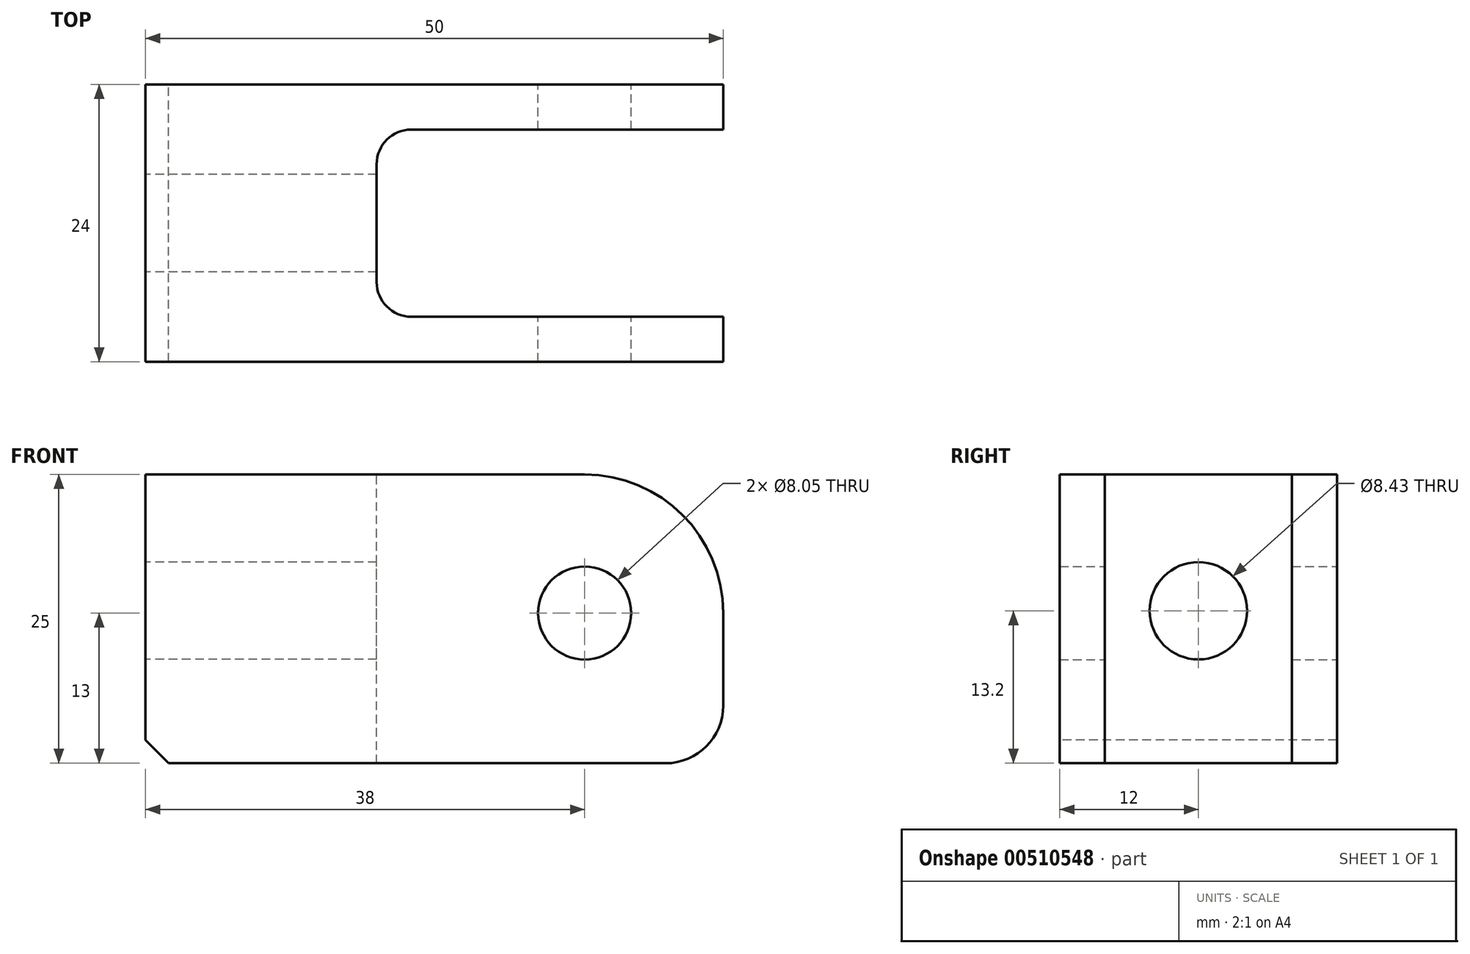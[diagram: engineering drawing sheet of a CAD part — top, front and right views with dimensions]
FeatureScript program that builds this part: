
annotation { "Feature Type Name" : "Feature", "Feature Type Description" : "" }
export const myFeature = defineFeature(function(context is Context, id is Id, definition is map)
    precondition{}
    {
        {
            var Q0;
            Q0=qCreatedBy(makeId("Front.planeOp"),FACE);
            var sketch = newSketch(context, id + "F0", { "sketchPlane" : qUnion([Q0])});
            skLineSegment(sketch, "E0.bottom", {"start": v(0, 0) * mm, "end": v(50, 0) * mm});
            skLineSegment(sketch, "E0.top", {"start": v(0, 25) * mm, "end": v(38, 25) * mm});
            skLineSegment(sketch, "E0.left", {"start": v(0, 0) * mm, "end": v(0, 25) * mm});
            skLineSegment(sketch, "E0.right", {"start": v(50, 0) * mm, "end": v(50, 13) * mm});
            skPoint(sketch, "E1.visualSharp", {"position": v(50, 25) * mm});
            skArc(sketch, "E1.filletArc", {"start": v(50, 13) * mm, "mid": v(46.49, 21.49) * mm, "end": v(38, 25) * mm});
            skCircle(sketch, "E2", {"center": v(38, 13) * mm, "radius": 4.03 * mm});
            skLineSegment(sketch, "E3.bottom", {"start": v(25, -10) * mm, "end": v(60, -10) * mm});
            skLineSegment(sketch, "E3.top", {"start": v(20, 40) * mm, "end": v(60, 40) * mm});
            skLineSegment(sketch, "E3.left", {"start": v(20, -5) * mm, "end": v(20, 40) * mm});
            skLineSegment(sketch, "E3.right", {"start": v(60, -10) * mm, "end": v(60, 40) * mm});
            skPoint(sketch, "E4.visualSharp", {"position": v(20, -10) * mm});
            skArc(sketch, "E4.filletArc", {"start": v(20, -5) * mm, "mid": v(21.46, -8.54) * mm, "end": v(25, -10) * mm});
            skSolve(sketch);
        }
        {
            var Q0;
            Q0=makeQuery(id+"F0.imprint","IMPRINT",FACE,{"disambiguationData":[TD([[makeQuery(id+"F0.imprint","IMPRINT",EDGE,{"derivedFrom":sQuery(id+"F0.wireOp",EDGE,"E0.bottom")}),1.0]])]});
            var Q1;
            {var subQ0=sQuery(id+"F0.wireOp",EDGE,"E1.filletArc");Q1=makeQuery(id+"F0.imprint","IMPRINT",FACE,{"disambiguationData":[TD([[makeQuery(id+"F0.imprint","IMPRINT",EDGE,{"derivedFrom":subQ0}),1.0]])]});}
            extrude(context, id + "F1", {"entities" : qUnion([Q0, Q1]), "depth" : 12 * mm, "hasSecondDirection" : true, "secondDirectionOppositeDirection" : true, "secondDirectionDepth" : 12 * mm});
        }
        {
            var Q0;
            {var subQ0=sQuery(id+"F0.wireOp",EDGE,"E1.filletArc");Q0=makeQuery(id+"F0.imprint","IMPRINT",FACE,{"disambiguationData":[TD([[makeQuery(id+"F0.imprint","IMPRINT",EDGE,{"derivedFrom":subQ0}),1.0]])]});}
            extrude(context, id + "F2", {"entities" : qUnion([Q0]), "operationType" : NewBodyOperationType.REMOVE, "oppositeDirection" : true, "depth" : 8.1 * mm, "hasSecondDirection" : true, "secondDirectionOppositeDirection" : false, "secondDirectionDepth" : 8.1 * mm, "offsetDistance" : 25 * mm});
        }
        {
            var Q0;
            Q0=makeQuery(id+"F2.boolean.opBoolean","COPY",EDGE,{"derivedFrom":makeQuery(id+"F2.opExtrude","CAP_EDGE",EDGE,{"disambiguationData":[OSD([sQuery(id+"F0.wireOp",EDGE,"E3.left")])],"isStart":true})});
            var Q1;
            Q1=makeQuery(id+"F2.boolean.opBoolean","COPY",EDGE,{"derivedFrom":makeQuery(id+"F2.opExtrude","CAP_EDGE",EDGE,{"disambiguationData":[OSD([sQuery(id+"F0.wireOp",EDGE,"E3.left")])],"isStart":false})});
            fillet(context, id + "F3", {"entities" : qUnion([Q0, Q1]), "radius" : 3 * mm, "tangentPropagation" : true, "allowEdgeOverflow" : false});
        }
        {
            var Q0;
            {var subQ0=sQuery(id+"F0.wireOp",EDGE,"E0.bottom");var subQ1=sQuery(id+"F0.wireOp",EDGE,"E0.right");var subQ2=sQuery(id+"F0.wireOp",EDGE,"E2");var subQ3=sQuery(id+"F0.wireOp",EDGE,"E1.filletArc");var subQ4=sQuery(id+"F0.wireOp",EDGE,"E0.top");Q0=makeQuery(id+"F2.boolean.opBoolean","SPLIT",EDGE,{"disambiguationData":[TD([makeQuery(id+"F1.opExtrude","CAP_FACE",FACE,{"disambiguationData":[OSD([subQ0,subQ4,sQuery(id+"F0.wireOp",EDGE,"E0.left"),subQ1,subQ3,subQ2])],"isStart":false})])],"derivedFrom":makeQuery(id+"F1.opExtrude","SWEPT_EDGE",EDGE,{"disambiguationData":[OSD([subQ0,subQ1])]})});}
            var Q1;
            {var subQ0=sQuery(id+"F0.wireOp",EDGE,"E0.bottom");var subQ1=sQuery(id+"F0.wireOp",EDGE,"E0.right");var subQ2=sQuery(id+"F0.wireOp",EDGE,"E2");var subQ3=sQuery(id+"F0.wireOp",EDGE,"E1.filletArc");var subQ4=sQuery(id+"F0.wireOp",EDGE,"E0.top");Q1=makeQuery(id+"F2.boolean.opBoolean","SPLIT",EDGE,{"disambiguationData":[TD([makeQuery(id+"F1.opExtrude","CAP_FACE",FACE,{"disambiguationData":[OSD([subQ0,subQ4,sQuery(id+"F0.wireOp",EDGE,"E0.left"),subQ1,subQ3,subQ2])],"isStart":true})])],"derivedFrom":makeQuery(id+"F1.opExtrude","SWEPT_EDGE",EDGE,{"disambiguationData":[OSD([subQ0,subQ1])]})});}
            fillet(context, id + "F4", {"entities" : qUnion([Q0, Q1]), "radius" : 5 * mm, "tangentPropagation" : true, "allowEdgeOverflow" : false});
        }
        {
            var Q0;
            Q0=makeQuery(id+"F1.opExtrude","SWEPT_FACE",FACE,{"disambiguationData":[OSD([sQuery(id+"F0.wireOp",EDGE,"E0.left")])]});
            var sketch = newSketch(context, id + "F5", { "sketchPlane" : qUnion([Q0])});
            skPoint(sketch, "E5", {"position": v(0, 13.2) * mm});
            skSolve(sketch);
        }
        {
            var Q0;
            Q0=sQuery(id+"F5.wireOp",VERTEX,"E5");
            var Q1;
            Q1=makeQuery(id+"F1.opExtrude","SWEPT_BODY",BODY,{"disambiguationData":[OSD([sQuery(id+"F0.wireOp",EDGE,"E0.bottom"),sQuery(id+"F0.wireOp",EDGE,"E0.top"),sQuery(id+"F0.wireOp",EDGE,"E0.left"),sQuery(id+"F0.wireOp",EDGE,"E0.right"),sQuery(id+"F0.wireOp",EDGE,"E1.filletArc"),sQuery(id+"F0.wireOp",EDGE,"E2")])]});
            hole(context, id + "F6", {"style" : HoleStyle.SIMPLE, "endStyle" : HoleEndStyle.BLIND, "standardTappedOrClearance" : lookupTablePath({ "standard" : "ANSI", "engagement" : "75%", "pitch" : "24 tpi", "size" : "3/8", "type" : "Tapped" }), "standardBlindInLast" : lookupTablePath({ "standard" : "ANSI", "engagement" : "75%", "pitch" : "24 tpi", "size" : "3/8", "type" : "Tapped" }), "holeDiameter" : 8.43 * mm, "showTappedDepth" : true, "holeDepth" : 30.8 * mm, "isTappedThrough" : true, "tappedDepth" : 27.62 * mm, "tapClearance" : 3, "locations" : qUnion([Q0]), "scope" : qUnion([Q1]), "majorDiameter" : 9.53 * mm});
        }
        {
            var Q0;
            Q0=makeQuery(id+"F1.opExtrude","SWEPT_EDGE",EDGE,{"disambiguationData":[OSD([sQuery(id+"F0.wireOp",EDGE,"E0.bottom"),sQuery(id+"F0.wireOp",EDGE,"E0.left")])]});
            chamfer(context, id + "F7", {"entities" : qUnion([Q0]), "width" : 2 * mm, "tangentPropagation" : true});
        }
    });
